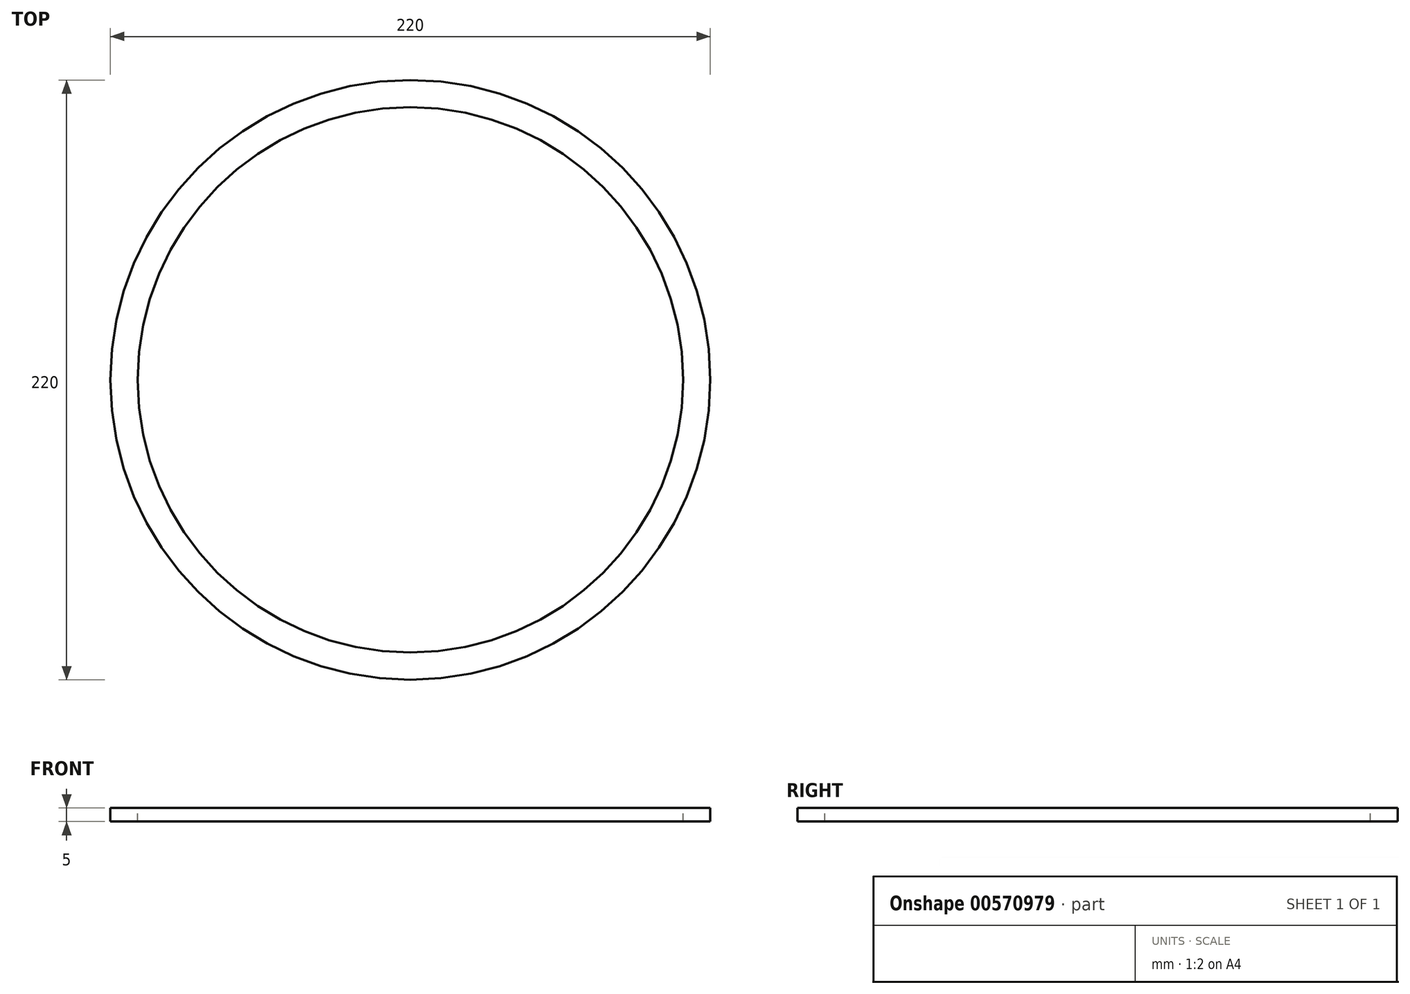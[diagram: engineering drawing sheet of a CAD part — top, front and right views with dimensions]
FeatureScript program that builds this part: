
annotation { "Feature Type Name" : "Feature", "Feature Type Description" : "" }
export const myFeature = defineFeature(function(context is Context, id is Id, definition is map)
    precondition{}
    {
        {
            var Q0;
            Q0=qCreatedBy(makeId("Top.planeOp"),FACE);
            var sketch = newSketch(context, id + "F0", { "sketchPlane" : qUnion([Q0])});
            skCircle(sketch, "E0", {"center": v(0, 0) * mm, "radius": 110 * mm});
            skCircle(sketch, "E1", {"center": v(0, 0) * mm, "radius": 100 * mm});
            skSolve(sketch);
        }
        {
            var Q0;
            Q0=sQuery(id+"F0.wireOp",EDGE,"E1");
            var Q1;
            Q1=sQuery(id+"F0.wireOp",EDGE,"E0");
            extrude(context, id + "F1", {"bodyType" : ToolBodyType.SURFACE, "surfaceEntities" : qUnion([Q0, Q1]), "depth" : 5 * mm, "offsetDistance" : 25 * mm});
        }
    });
